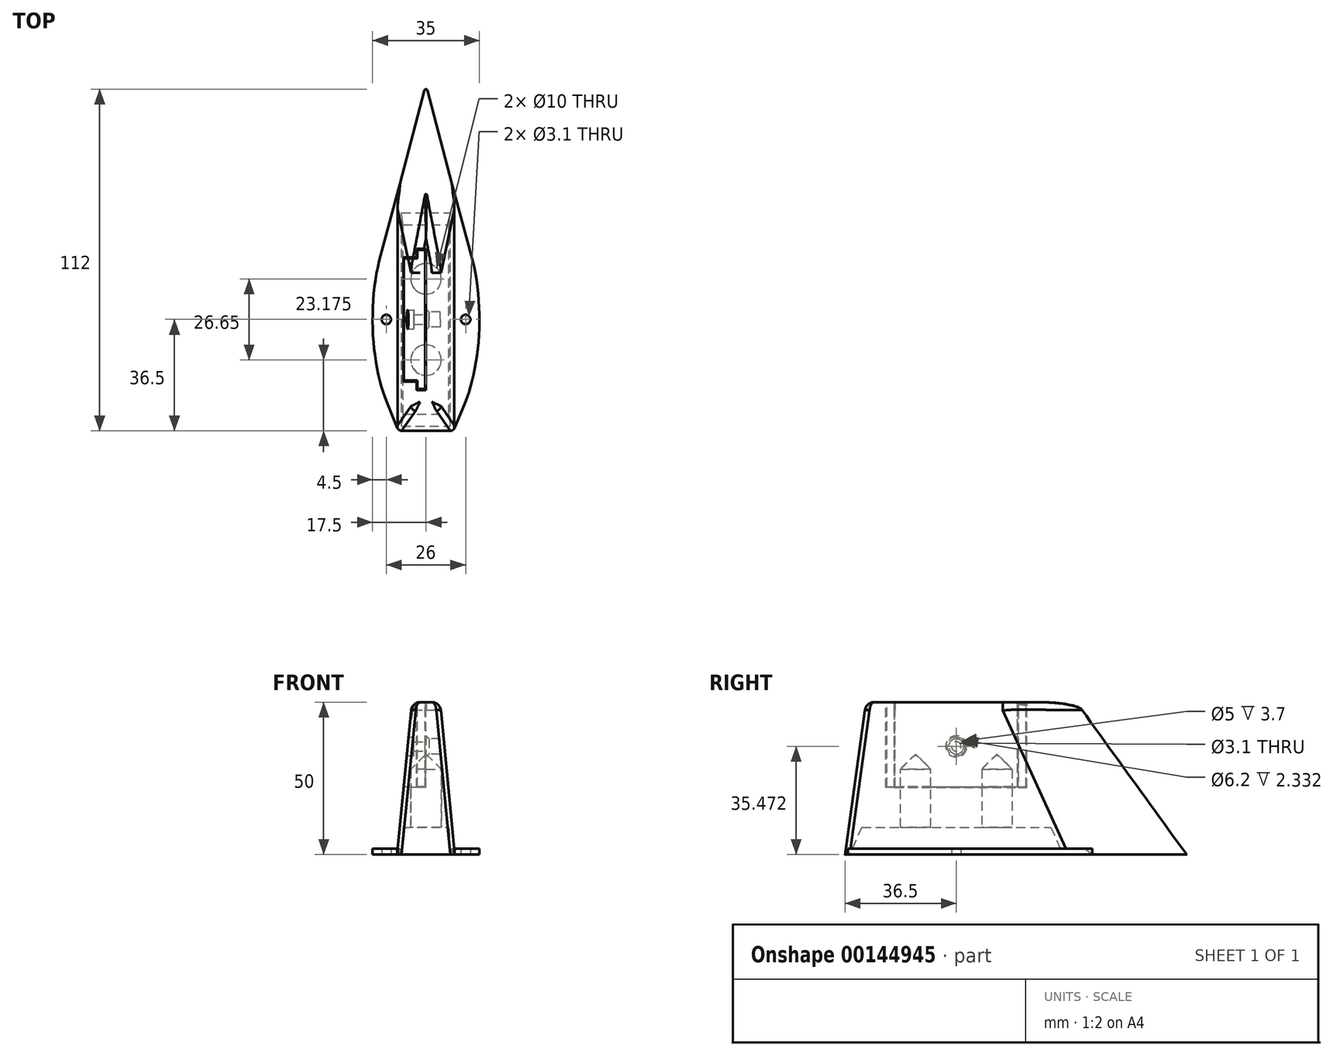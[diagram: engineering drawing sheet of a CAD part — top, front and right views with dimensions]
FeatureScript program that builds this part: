
annotation { "Feature Type Name" : "Feature", "Feature Type Description" : "" }
export const myFeature = defineFeature(function(context is Context, id is Id, definition is map)
    precondition{}
    {
        {
            var Q0;
            Q0=qCreatedBy(makeId("Top.planeOp"),FACE);
            var sketch = newSketch(context, id + "F0", { "sketchPlane" : qUnion([Q0])});
            skPoint(sketch, "E0.middle", {"position": v(0, 0) * mm});
            skLineSegment(sketch, "E1", {"start": v(-0.48, 75.13) * mm, "end": v(-8.52, 44.52) * mm});
            skLineSegment(sketch, "E2.MirrorCS", {"start": v(0.48, 75.13) * mm, "end": v(8.52, 44.52) * mm});
            skPoint(sketch, "E3.visualSharp", {"position": v(0, 76.97) * mm});
            skArc(sketch, "E3.filletArc", {"start": v(0.48, 75.13) * mm, "mid": v(0, 75.5) * mm, "end": v(-0.48, 75.13) * mm});
            skLineSegment(sketch, "E4", {"start": v(-9.5, 36.9) * mm, "end": v(-9.5, -35) * mm});
            skLineSegment(sketch, "E5", {"start": v(-8, -36.5) * mm, "end": v(8, -36.5) * mm});
            skLineSegment(sketch, "E6.MirrorCS", {"start": v(9.5, 36.9) * mm, "end": v(9.5, -35) * mm});
            skPoint(sketch, "E7.visualSharp", {"position": v(-9.5, 40.77) * mm});
            skArc(sketch, "E7.filletArc", {"start": v(-8.52, 44.52) * mm, "mid": v(-9.25, 40.74) * mm, "end": v(-9.5, 36.9) * mm});
            skPoint(sketch, "E8.visualSharp", {"position": v(9.5, 40.77) * mm});
            skArc(sketch, "E8.filletArc", {"start": v(9.5, 36.9) * mm, "mid": v(9.25, 40.74) * mm, "end": v(8.52, 44.52) * mm});
            skPoint(sketch, "E9.visualSharp", {"position": v(9.5, -36.5) * mm});
            skArc(sketch, "E9.filletArc", {"start": v(8, -36.5) * mm, "mid": v(9.06, -36.06) * mm, "end": v(9.5, -35) * mm});
            skPoint(sketch, "E10.visualSharp", {"position": v(-9.5, -36.5) * mm});
            skArc(sketch, "E10.filletArc", {"start": v(-9.5, -35) * mm, "mid": v(-9.06, -36.06) * mm, "end": v(-8, -36.5) * mm});
            skSolve(sketch);
        }
        {
            var Q0;
            Q0=qCreatedBy(makeId("Top.planeOp"),FACE);
            cPlane(context, id + "F1", {"entities" : qUnion([Q0]), "cplaneType" : CPlaneType.OFFSET, "offset" : 50 * mm, "width" : 150 * mm, "height" : 150 * mm});
        }
        {
            var Q0;
            Q0=qCreatedBy(id+"F1.planeOp",FACE);
            var sketch = newSketch(context, id + "F2", { "sketchPlane" : qUnion([Q0])});
            skLineSegment(sketch, "E11", {"start": v(-4.6, 14.01) * mm, "end": v(-4.6, -28.06) * mm});
            skLineSegment(sketch, "E12", {"start": v(-4.26, 17.7) * mm, "end": v(-0.25, 39.13) * mm});
            skLineSegment(sketch, "E13.MirrorCS", {"start": v(4.6, 14.01) * mm, "end": v(4.6, -28.06) * mm});
            skLineSegment(sketch, "E14.MirrorCS", {"start": v(4.26, 17.7) * mm, "end": v(0.25, 39.13) * mm});
            skPoint(sketch, "E15.visualSharp", {"position": v(-4.6, 15.87) * mm});
            skArc(sketch, "E15.filletArc", {"start": v(-4.26, 17.7) * mm, "mid": v(-4.52, 15.86) * mm, "end": v(-4.6, 14.01) * mm});
            skPoint(sketch, "E16.visualSharp", {"position": v(4.6, 15.87) * mm});
            skArc(sketch, "E16.filletArc", {"start": v(4.6, 14.01) * mm, "mid": v(4.52, 15.86) * mm, "end": v(4.26, 17.7) * mm});
            skPoint(sketch, "E17.visualSharp", {"position": v(4.6, -29.56) * mm});
            skArc(sketch, "E17.filletArc", {"start": v(3.1, -29.56) * mm, "mid": v(4.17, -29.12) * mm, "end": v(4.6, -28.06) * mm});
            skPoint(sketch, "E18.visualSharp", {"position": v(-4.6, -29.56) * mm});
            skArc(sketch, "E18.filletArc", {"start": v(-4.6, -28.06) * mm, "mid": v(-4.17, -29.12) * mm, "end": v(-3.1, -29.56) * mm});
            skPoint(sketch, "E19.visualSharp", {"position": v(0, 40.44) * mm});
            skArc(sketch, "E19.filletArc", {"start": v(0.25, 39.13) * mm, "mid": v(0, 39.34) * mm, "end": v(-0.25, 39.13) * mm});
            skLineSegment(sketch, "E20", {"start": v(-3.1, -29.56) * mm, "end": v(3.1, -29.56) * mm});
            skSolve(sketch);
        }
        {
            var Q0;
            Q0 = qSketchRegion(id + "F0", true);
            var Q1;
            Q1 = qSketchRegion(id + "F2", true);
            var Q2;
            Q2=sQuery(id+"F0.wireOp",VERTEX,"E3.filletArc.start");
            var Q3;
            Q3=sQuery(id+"F2.wireOp",VERTEX,"E19.filletArc.start");
            loft(context, id + "F3", {"sheetProfilesArray" : [{ "sheetProfileEntities" : qUnion([Q0]) }, { "sheetProfileEntities" : qUnion([Q1]) }], "matchConnections" : true, "connections" : [{ "connectionEntities" : qUnion([Q2, Q3]), "connectionEdgeQueries" : qUnion([]), "connectionEdgeParameters" : [] }]});
        }
        {
            var Q0;
            Q0=makeQuery(id+"F0.imprint","IMPRINT",FACE,{"disambiguationData":[TD([[makeQuery(id+"F0.imprint","IMPRINT",EDGE,{"derivedFrom":sQuery(id+"F0.wireOp",EDGE,"E1")}),1.0]])]});
            var sketch = newSketch(context, id + "F4", { "sketchPlane" : qUnion([Q0])});
            skLineSegment(sketch, "E21.bottom", {"start": v(-8, -35) * mm, "end": v(8, -35) * mm});
            skLineSegment(sketch, "E21.top", {"start": v(-8, 35) * mm, "end": v(8, 35) * mm});
            skLineSegment(sketch, "E21.left", {"start": v(-8, -35) * mm, "end": v(-8, 35) * mm});
            skLineSegment(sketch, "E21.right", {"start": v(8, -35) * mm, "end": v(8, 35) * mm});
            skPoint(sketch, "E21.middle", {"position": v(0, 0) * mm});
            skSolve(sketch);
        }
        {
            var Q0;
            Q0=makeQuery(id+"F0.imprint","IMPRINT",FACE,{"disambiguationData":[TD([[makeQuery(id+"F0.imprint","IMPRINT",EDGE,{"derivedFrom":sQuery(id+"F0.wireOp",EDGE,"E1")}),1.0]])]});
            cPlane(context, id + "F5", {"entities" : qUnion([Q0]), "cplaneType" : CPlaneType.OFFSET, "offset" : 9 * mm, "width" : 150 * mm, "height" : 150 * mm});
        }
        {
            var Q0;
            Q0=qCreatedBy(id+"F5.planeOp",FACE);
            var sketch = newSketch(context, id + "F6", { "sketchPlane" : qUnion([Q0])});
            skLineSegment(sketch, "E22.bottom", {"start": v(-7.5, -31) * mm, "end": v(7.5, -31) * mm});
            skLineSegment(sketch, "E22.top", {"start": v(-7.5, 31) * mm, "end": v(7.5, 31) * mm});
            skLineSegment(sketch, "E22.left", {"start": v(-7.5, -31) * mm, "end": v(-7.5, 31) * mm});
            skLineSegment(sketch, "E22.right", {"start": v(7.5, -31) * mm, "end": v(7.5, 31) * mm});
            skPoint(sketch, "E22.middle", {"position": v(0, 0) * mm});
            skSolve(sketch);
        }
        {
            var Q1;
            Q1 = qSketchRegion(id + "F6", true);
            var Q2;
            Q2 = qSketchRegion(id + "F4", true);
            loft(context, id + "F7", {"operationType" : NewBodyOperationType.REMOVE, "sheetProfilesArray" : [{ "sheetProfileEntities" : qUnion([Q1]) }, { "sheetProfileEntities" : qUnion([Q2]) }]});
        }
        {
            var Q0;
            Q0=qCreatedBy(makeId("Right.planeOp"),FACE);
            var sketch = newSketch(context, id + "F8", { "sketchPlane" : qUnion([Q0])});
            skLineSegment(sketch, "E23", {"start": v(-13.32, 50) * mm, "end": v(-13.32, 9) * mm});
            skLineSegment(sketch, "E24.MirrorCS", {"start": v(13.32, 50) * mm, "end": v(13.32, 9) * mm});
            skLineSegment(sketch, "E25.bottom", {"start": v(-13.33, 33) * mm, "end": v(-18.33, 33) * mm});
            skLineSegment(sketch, "E25.top", {"start": v(-13.32, 9) * mm, "end": v(-18.32, 9) * mm});
            skLineSegment(sketch, "E25.left", {"start": v(-13.32, 33) * mm, "end": v(-13.32, 9) * mm});
            skLineSegment(sketch, "E25.right", {"start": v(-18.33, 33) * mm, "end": v(-18.32, 9) * mm});
            skLineSegment(sketch, "E26.bottom", {"start": v(-13.33, 33) * mm, "end": v(-16.33, 33) * mm});
            skLineSegment(sketch, "E26.top", {"start": v(-13.33, 50) * mm, "end": v(-16.33, 50) * mm});
            skLineSegment(sketch, "E26.left", {"start": v(-13.33, 33) * mm, "end": v(-13.33, 50) * mm});
            skLineSegment(sketch, "E26.right", {"start": v(-16.33, 33) * mm, "end": v(-16.33, 50) * mm});
            skLineSegment(sketch, "E27.MirrorCS", {"start": v(13.33, 33) * mm, "end": v(18.33, 33) * mm});
            skLineSegment(sketch, "E28.MirrorCS", {"start": v(18.33, 33) * mm, "end": v(18.32, 9) * mm});
            skLineSegment(sketch, "E29.MirrorCS", {"start": v(13.33, 33) * mm, "end": v(16.33, 33) * mm});
            skLineSegment(sketch, "E30.MirrorCS", {"start": v(13.32, 33) * mm, "end": v(13.32, 9) * mm});
            skLineSegment(sketch, "E31.MirrorCS", {"start": v(13.33, 50) * mm, "end": v(16.33, 50) * mm});
            skLineSegment(sketch, "E32.MirrorCS", {"start": v(13.33, 33) * mm, "end": v(13.33, 50) * mm});
            skLineSegment(sketch, "E33.MirrorCS", {"start": v(16.33, 33) * mm, "end": v(16.33, 50) * mm});
            skLineSegment(sketch, "E34.MirrorCS", {"start": v(13.32, 9) * mm, "end": v(18.32, 9) * mm});
            skSolve(sketch);
        }
        {
            var Q0;
            Q0=makeQuery(id+"F8.imprint","IMPRINT",FACE,{"disambiguationData":[TD([[makeQuery(id+"F8.imprint","IMPRINT",EDGE,{"derivedFrom":sQuery(id+"F8.wireOp",EDGE,"E26.bottom")}),-1.0]])]});
            var Q1;
            Q1=makeQuery(id+"F8.imprint","IMPRINT",FACE,{"disambiguationData":[TD([[makeQuery(id+"F8.imprint","IMPRINT",EDGE,{"derivedFrom":sQuery(id+"F8.wireOp",EDGE,"E25.bottom")}),1.0]])]});
            var Q2;
            Q2=sQuery(id+"F8.wireOp",EDGE,"E26.left");
            revolve(context, id + "F9", {"operationType" : NewBodyOperationType.REMOVE, "entities" : qUnion([Q0, Q1]), "axis" : qUnion([Q2]), "revolveType" : RevolveType.FULL, "oppositeDirection" : true});
        }
        {
            var Q0;
            Q0=makeQuery(id+"F8.imprint","IMPRINT",FACE,{"disambiguationData":[TD([[makeQuery(id+"F8.imprint","IMPRINT",EDGE,{"derivedFrom":sQuery(id+"F8.wireOp",EDGE,"E27.MirrorCS")}),-1.0]])]});
            var Q1;
            Q1=makeQuery(id+"F8.imprint","IMPRINT",FACE,{"disambiguationData":[TD([[makeQuery(id+"F8.imprint","IMPRINT",EDGE,{"derivedFrom":sQuery(id+"F8.wireOp",EDGE,"E29.MirrorCS")}),1.0]])]});
            var Q2;
            Q2=sQuery(id+"F8.wireOp",EDGE,"E24.MirrorCS");
            revolve(context, id + "F10", {"operationType" : NewBodyOperationType.REMOVE, "entities" : qUnion([Q0, Q1]), "axis" : qUnion([Q2]), "revolveType" : RevolveType.FULL, "oppositeDirection" : true});
        }
        {
            var Q0;
            Q0=makeQuery(id+"F3.opLoft","MID_CAP_EDGE",EDGE,{"disambiguationData":[OSD([sQuery(id+"F2.wireOp",EDGE,"E13.MirrorCS"),sQuery(id+"F2.wireOp",EDGE,"E16.filletArc"),sQuery(id+"F2.wireOp",EDGE,"E17.filletArc")])],"capPos":1.0});
            fillet(context, id + "F11", {"entities" : qUnion([Q0]), "radius" : 3 * mm, "tangentPropagation" : true, "allowEdgeOverflow" : false});
        }
        {
            var Q0;
            Q0=makeQuery(id+"F3.opLoft","CAP_FACE",FACE,{"disambiguationData":[OSD([makeQuery(id+"F0.imprint","IMPRINT",FACE,{"disambiguationData":[TD([[makeQuery(id+"F0.imprint","IMPRINT",EDGE,{"derivedFrom":sQuery(id+"F0.wireOp",EDGE,"E1")}),1.0]])]})])],"isStart":true});
            var sketch = newSketch(context, id + "F12", { "sketchPlane" : qUnion([Q0])});
            skCircle(sketch, "E35", {"center": v(13, 0) * mm, "radius": 1.55 * mm});
            skCircle(sketch, "E36.MirrorC", {"center": v(-13, 0) * mm, "radius": 1.55 * mm});
            skFitSpline(sketch, "E37.0", {"points": [v(9.5, -36.9) * mm, v(9.5, -37.51) * mm, v(9.46, -38.8) * mm, v(9.2, -41.45) * mm, v(8.82, -43.38) * mm, v(8.52, -44.52) * mm]});
            skFitSpline(sketch, "E38.0", {"points": [v(-8.52, -44.52) * mm, v(-8.82, -43.38) * mm, v(-9.2, -41.45) * mm, v(-9.46, -38.8) * mm, v(-9.5, -37.51) * mm, v(-9.5, -36.9) * mm]});
            skLineSegment(sketch, "E39.0", {"start": v(-9.5, -36.9) * mm, "end": v(-9.5, 35) * mm});
            skFitSpline(sketch, "E40.0", {"points": [v(8, 36.5) * mm, v(8.25, 36.5) * mm, v(8.67, 36.38) * mm, v(9.1, 36.06) * mm, v(9.4, 35.62) * mm, v(9.5, 35.23) * mm, v(9.5, 35) * mm]});
            skFitSpline(sketch, "E41.0", {"points": [v(-9.5, 35) * mm, v(-9.5, 35.23) * mm, v(-9.4, 35.62) * mm, v(-9.1, 36.06) * mm, v(-8.67, 36.38) * mm, v(-8.25, 36.5) * mm, v(-8, 36.5) * mm]});
            skEllipticalArc(sketch, "E42", {});
            skLineSegment(sketch, "E43", {"start": v(8.52, -44.52) * mm, "end": v(14.87, -21.07) * mm});
            skLineSegment(sketch, "E44.MirrorCS", {"start": v(-8.52, -44.52) * mm, "end": v(-14.87, -21.07) * mm});
            skLineSegment(sketch, "E45", {"start": v(12.75, 27.4) * mm, "end": v(9.39, 35.57) * mm});
            skLineSegment(sketch, "E46.MirrorCS", {"start": v(-12.75, 27.4) * mm, "end": v(-9.39, 35.57) * mm});
            skPoint(sketch, "E47.orphan", {"position": v(-8, 36.5) * mm});
            skPoint(sketch, "E48.orphan", {"position": v(8, 36.5) * mm});
            skEllipticalArc(sketch, "E49.trimOffspring", {});
            skLineSegment(sketch, "E50.0", {"start": v(9, 35) * mm, "end": v(9, -36.9) * mm});
            skLineSegment(sketch, "E51", {"start": v(9.39, 35.57) * mm, "end": v(9, 35) * mm});
            skLineSegment(sketch, "E52", {"start": v(8.52, -44.52) * mm, "end": v(9, -36.9) * mm});
            skLineSegment(sketch, "E53.MirrorCS", {"start": v(-9, 35) * mm, "end": v(-9, -36.9) * mm});
            skLineSegment(sketch, "E54.MirrorCS", {"start": v(-8.52, -44.52) * mm, "end": v(-9, -36.9) * mm});
            skLineSegment(sketch, "E55.MirrorCS", {"start": v(-9.39, 35.57) * mm, "end": v(-9, 35) * mm});
            const initialGuessF12  = {"E42": [0, 0, 0, 1, 0.04, 0.0175, 0.8160046856801231, 2.1256548198851757], "E49.trimOffspring": [0, 0, 0, 1, 0.04, 0.0175, 4.1575304872944105, 5.467180621499463]};
            skSetInitialGuess(sketch, initialGuessF12);
            skSolve(sketch);
        }
        {
            var Q0;
            Q0 = qSketchRegion(id + "F12", true);
            extrude(context, id + "F13", {"entities" : qUnion([Q0]), "operationType" : NewBodyOperationType.ADD, "oppositeDirection" : true, "depth" : 2 * mm});
        }
        {
            var Q0;
            Q0=makeQuery(id+"F10.boolean.opBoolean","COPY",EDGE,{"derivedFrom":makeQuery(id+"F10.opRevolve","SWEPT_EDGE",EDGE,{"disambiguationData":[OSD([sQuery(id+"F8.wireOp",EDGE,"E27.MirrorCS"),sQuery(id+"F8.wireOp",EDGE,"E29.MirrorCS"),sQuery(id+"F8.wireOp",EDGE,"E33.MirrorCS")])]})});
            var Q1;
            Q1=makeQuery(id+"F9.boolean.opBoolean","COPY",EDGE,{"derivedFrom":makeQuery(id+"F9.opRevolve","SWEPT_EDGE",EDGE,{"disambiguationData":[OSD([sQuery(id+"F8.wireOp",EDGE,"E25.bottom"),sQuery(id+"F8.wireOp",EDGE,"E26.bottom"),sQuery(id+"F8.wireOp",EDGE,"E26.right")])]})});
            chamfer(context, id + "F14", {"entities" : qUnion([Q0, Q1]), "width" : 5 * mm, "tangentPropagation" : true});
        }
        {
            var Q0;
            Q0=makeQuery(id+"F11.opFillet","SPLIT",FACE,{"disambiguationData":[OD(2.0)],"derivedFrom":makeQuery(id+"F3.opLoft","CAP_FACE",FACE,{"disambiguationData":[OSD([makeQuery(id+"F2.imprint","IMPRINT",FACE,{"disambiguationData":[TD([[makeQuery(id+"F2.imprint","IMPRINT",EDGE,{"derivedFrom":sQuery(id+"F2.wireOp",EDGE,"E11")}),1.0]])]})])],"isStart":true})});
            var sketch = newSketch(context, id + "F15", { "sketchPlane" : qUnion([Q0])});
            skLineSegment(sketch, "E56.left", {"start": v(0, 20.7) * mm, "end": v(0, -20.3) * mm});
            skLineSegment(sketch, "E56.right", {"start": v(-0.3, 20.3) * mm, "end": v(-0.3, -20.3) * mm});
            skLineSegment(sketch, "E57", {"start": v(0, 22.84) * mm, "end": v(0, 20.7) * mm});
            skLineSegment(sketch, "E58", {"start": v(-0.3, 20.3) * mm, "end": v(-0.3, 22.8) * mm});
            skLineSegment(sketch, "E59", {"start": v(-0.3, 22.8) * mm, "end": v(-2.8, 22.8) * mm});
            skLineSegment(sketch, "E60", {"start": v(-2.8, 22.8) * mm, "end": v(-2.8, 20.3) * mm});
            skLineSegment(sketch, "E61", {"start": v(-3.1, 20.34) * mm, "end": v(-3.1, 23.14) * mm});
            skLineSegment(sketch, "E62", {"start": v(0, 22.84) * mm, "end": v(0, 23.14) * mm});
            skLineSegment(sketch, "E63", {"start": v(0, 23.14) * mm, "end": v(-3.1, 23.14) * mm});
            skLineSegment(sketch, "E64", {"start": v(-3.1, 20.34) * mm, "end": v(-10.14, 20.34) * mm});
            skLineSegment(sketch, "E65", {"start": v(-10.14, 20.34) * mm, "end": v(-10.14, 20.04) * mm});
            skLineSegment(sketch, "E66", {"start": v(-10.14, 20.04) * mm, "end": v(-2.8, 20.04) * mm});
            skLineSegment(sketch, "E67", {"start": v(-2.8, 20.04) * mm, "end": v(-2.8, 20.3) * mm});
            skLineSegment(sketch, "E68.MirrorCS", {"start": v(0, -22.84) * mm, "end": v(0, -23.14) * mm});
            skLineSegment(sketch, "E69.MirrorCS", {"start": v(-2.8, -20.04) * mm, "end": v(-2.8, -20.3) * mm});
            skLineSegment(sketch, "E70.MirrorCS", {"start": v(-10.14, -20.34) * mm, "end": v(-10.14, -20.04) * mm});
            skLineSegment(sketch, "E71.MirrorCS", {"start": v(-3.1, -20.34) * mm, "end": v(-3.1, -23.14) * mm});
            skLineSegment(sketch, "E72.MirrorCS", {"start": v(0, -22.84) * mm, "end": v(0, -20.7) * mm});
            skLineSegment(sketch, "E73.MirrorCS", {"start": v(0, -23.14) * mm, "end": v(-3.1, -23.14) * mm});
            skLineSegment(sketch, "E74.MirrorCS", {"start": v(-0.3, -20.3) * mm, "end": v(-0.3, -22.8) * mm});
            skLineSegment(sketch, "E75.MirrorCS", {"start": v(-2.8, -22.8) * mm, "end": v(-2.8, -20.3) * mm});
            skLineSegment(sketch, "E76.MirrorCS", {"start": v(-3.1, -20.34) * mm, "end": v(-10.14, -20.34) * mm});
            skLineSegment(sketch, "E77.MirrorCS", {"start": v(-10.14, -20.04) * mm, "end": v(-2.8, -20.04) * mm});
            skLineSegment(sketch, "E78.MirrorCS", {"start": v(-0.3, -22.8) * mm, "end": v(-2.8, -22.8) * mm});
            skLineSegment(sketch, "E79", {"start": v(0, -20.3) * mm, "end": v(0, -20.7) * mm});
            skSolve(sketch);
        }
        {
            var Q0;
            Q0 = qSketchRegion(id + "F15", true);
            extrude(context, id + "F16", {"entities" : qUnion([Q0]), "operationType" : NewBodyOperationType.REMOVE, "oppositeDirection" : true, "depth" : 28 * mm});
        }
        {
            var Q0;
            {var subQ0=sQuery(id+"F15.wireOp",EDGE,"E74.MirrorCS");var subQ1=sQuery(id+"F15.wireOp",EDGE,"E58");var subQ2=sQuery(id+"F15.wireOp",EDGE,"E56.right");var subQ3=sQuery(id+"F15.wireOp",EDGE,"E73.MirrorCS");var subQ4=sQuery(id+"F15.wireOp",EDGE,"E79");var subQ5=sQuery(id+"F15.wireOp",EDGE,"E72.MirrorCS");var subQ6=sQuery(id+"F15.wireOp",EDGE,"E68.MirrorCS");var subQ7=sQuery(id+"F15.wireOp",EDGE,"E62");var subQ8=sQuery(id+"F15.wireOp",EDGE,"E57");var subQ9=sQuery(id+"F15.wireOp",EDGE,"E56.left");var subQ10=sQuery(id+"F15.wireOp",EDGE,"E71.MirrorCS");var subQ11=sQuery(id+"F15.wireOp",EDGE,"E75.MirrorCS");var subQ12=sQuery(id+"F15.wireOp",EDGE,"E69.MirrorCS");var subQ13=sQuery(id+"F15.wireOp",EDGE,"E76.MirrorCS");var subQ14=sQuery(id+"F15.wireOp",EDGE,"E77.MirrorCS");var subQ15=sQuery(id+"F15.wireOp",EDGE,"E78.MirrorCS");Q0=makeQuery(id+"F16.boolean.opBoolean","COPY",FACE,{"disambiguationData":[TD([makeQuery(id+"F3.opLoft","SWEPT_FACE",FACE,{"disambiguationData":[OSD([sQuery(id+"F0.wireOp",EDGE,"E4"),sQuery(id+"F0.wireOp",EDGE,"E7.filletArc"),sQuery(id+"F0.wireOp",EDGE,"E10.filletArc"),sQuery(id+"F2.wireOp",EDGE,"E11"),sQuery(id+"F2.wireOp",EDGE,"E15.filletArc"),sQuery(id+"F2.wireOp",EDGE,"E18.filletArc")])]}),makeQuery(id+"F9.boolean.opBoolean","COPY",FACE,{"derivedFrom":makeQuery(id+"F9.opRevolve","SWEPT_FACE",FACE,{"disambiguationData":[OSD([sQuery(id+"F8.wireOp",EDGE,"E25.right")])]})}),makeQuery(id+"F16.opExtrude","SWEPT_FACE",FACE,{"disambiguationData":[OSD([subQ9,subQ8,subQ7,subQ6,subQ5,subQ4])]}),makeQuery(id+"F16.opExtrude","SWEPT_FACE",FACE,{"disambiguationData":[OSD([subQ2,subQ1,subQ0])]}),makeQuery(id+"F16.opExtrude","SWEPT_FACE",FACE,{"disambiguationData":[OSD([subQ12,subQ11])]}),makeQuery(id+"F16.opExtrude","SWEPT_FACE",FACE,{"disambiguationData":[OSD([subQ10])]}),makeQuery(id+"F16.opExtrude","SWEPT_FACE",FACE,{"disambiguationData":[OSD([subQ3])]}),makeQuery(id+"F16.opExtrude","SWEPT_FACE",FACE,{"disambiguationData":[OSD([subQ13])]}),makeQuery(id+"F16.opExtrude","SWEPT_FACE",FACE,{"disambiguationData":[OSD([subQ14])]}),makeQuery(id+"F16.opExtrude","SWEPT_FACE",FACE,{"disambiguationData":[OSD([subQ15])]})])],"derivedFrom":makeQuery(id+"F16.opExtrude","CAP_FACE",FACE,{"disambiguationData":[OSD([subQ9,subQ2,subQ8,subQ1,sQuery(id+"F15.wireOp",EDGE,"E59"),sQuery(id+"F15.wireOp",EDGE,"E60"),sQuery(id+"F15.wireOp",EDGE,"E61"),subQ7,sQuery(id+"F15.wireOp",EDGE,"E63"),sQuery(id+"F15.wireOp",EDGE,"E64"),sQuery(id+"F15.wireOp",EDGE,"E65"),sQuery(id+"F15.wireOp",EDGE,"E66"),sQuery(id+"F15.wireOp",EDGE,"E67"),subQ6,subQ12,sQuery(id+"F15.wireOp",EDGE,"E70.MirrorCS"),subQ10,subQ5,subQ3,subQ0,subQ11,subQ13,subQ14,subQ15,subQ4])],"isStart":false})});}
            var sketch = newSketch(context, id + "F17", { "sketchPlane" : qUnion([Q0])});
            skLineSegment(sketch, "E80", {"start": v(-2.8, -20.04) * mm, "end": v(-10.13, -20.04) * mm});
            skPoint(sketch, "E80.endSnap0", {"position": v(-5.07, -20.04) * mm});
            skLineSegment(sketch, "E81", {"start": v(-10.13, -20.04) * mm, "end": v(-10.13, 20.04) * mm});
            skLineSegment(sketch, "E82", {"start": v(-10.13, 20.04) * mm, "end": v(-2.8, 20.04) * mm});
            skLineSegment(sketch, "E83", {"start": v(-2.8, 20.04) * mm, "end": v(-2.8, 22.8) * mm});
            skLineSegment(sketch, "E84", {"start": v(-2.8, 22.8) * mm, "end": v(-0.3, 22.8) * mm});
            skLineSegment(sketch, "E85", {"start": v(-0.3, 22.8) * mm, "end": v(-0.3, -22.8) * mm});
            skLineSegment(sketch, "E86", {"start": v(-0.3, -22.8) * mm, "end": v(-2.8, -22.8) * mm});
            skLineSegment(sketch, "E87", {"start": v(-2.8, -22.8) * mm, "end": v(-2.8, -20.04) * mm});
            skSolve(sketch);
        }
        {
            var Q0;
            Q0 = qSketchRegion(id + "F17", true);
            extrude(context, id + "F18", {"entities" : qUnion([Q0]), "operationType" : NewBodyOperationType.REMOVE, "depth" : .3 * mm});
        }
        {
            var Q0;
            {var subQ0=sQuery(id+"F8.wireOp",EDGE,"E26.right");var subQ1=sQuery(id+"F15.wireOp",EDGE,"E74.MirrorCS");var subQ2=sQuery(id+"F15.wireOp",EDGE,"E58");var subQ3=sQuery(id+"F15.wireOp",EDGE,"E56.right");var subQ4=sQuery(id+"F8.wireOp",EDGE,"E33.MirrorCS");Q0=makeQuery(id+"F16.boolean.opBoolean","COPY",FACE,{"disambiguationData":[TD([makeQuery(id+"F3.opLoft","CAP_FACE",FACE,{"disambiguationData":[OSD([makeQuery(id+"F2.imprint","IMPRINT",FACE,{"disambiguationData":[TD([[makeQuery(id+"F2.imprint","IMPRINT",EDGE,{"derivedFrom":sQuery(id+"F2.wireOp",EDGE,"E11")}),1.0]])]})])],"isStart":true}),makeQuery(id+"F9.boolean.opBoolean","COPY",FACE,{"derivedFrom":makeQuery(id+"F9.opRevolve","SWEPT_FACE",FACE,{"disambiguationData":[OSD([sQuery(id+"F8.wireOp",EDGE,"E25.right")])]})}),makeQuery(id+"F9.boolean.opBoolean","COPY",FACE,{"derivedFrom":makeQuery(id+"F9.opRevolve","SWEPT_FACE",FACE,{"disambiguationData":[OSD([subQ0])]})}),makeQuery(id+"F10.boolean.opBoolean","COPY",FACE,{"derivedFrom":makeQuery(id+"F10.opRevolve","SWEPT_FACE",FACE,{"disambiguationData":[OSD([sQuery(id+"F8.wireOp",EDGE,"E28.MirrorCS")])]})}),makeQuery(id+"F10.boolean.opBoolean","COPY",FACE,{"derivedFrom":makeQuery(id+"F10.opRevolve","SWEPT_FACE",FACE,{"disambiguationData":[OSD([subQ4])]})}),makeQuery(id+"F14.opChamfer","BLEND_FACE",FACE,{"disambiguationData":[OSD([sQuery(id+"F8.wireOp",EDGE,"E25.bottom"),sQuery(id+"F8.wireOp",EDGE,"E26.bottom"),subQ0])]}),makeQuery(id+"F14.opChamfer","BLEND_FACE",FACE,{"disambiguationData":[OSD([sQuery(id+"F8.wireOp",EDGE,"E27.MirrorCS"),sQuery(id+"F8.wireOp",EDGE,"E29.MirrorCS"),subQ4])]}),makeQuery(id+"F16.opExtrude","CAP_FACE",FACE,{"disambiguationData":[OSD([sQuery(id+"F15.wireOp",EDGE,"E56.left"),subQ3,sQuery(id+"F15.wireOp",EDGE,"E57"),subQ2,sQuery(id+"F15.wireOp",EDGE,"E59"),sQuery(id+"F15.wireOp",EDGE,"E60"),sQuery(id+"F15.wireOp",EDGE,"E61"),sQuery(id+"F15.wireOp",EDGE,"E62"),sQuery(id+"F15.wireOp",EDGE,"E63"),sQuery(id+"F15.wireOp",EDGE,"E64"),sQuery(id+"F15.wireOp",EDGE,"E65"),sQuery(id+"F15.wireOp",EDGE,"E66"),sQuery(id+"F15.wireOp",EDGE,"E67"),sQuery(id+"F15.wireOp",EDGE,"E68.MirrorCS"),sQuery(id+"F15.wireOp",EDGE,"E69.MirrorCS"),sQuery(id+"F15.wireOp",EDGE,"E70.MirrorCS"),sQuery(id+"F15.wireOp",EDGE,"E71.MirrorCS"),sQuery(id+"F15.wireOp",EDGE,"E72.MirrorCS"),sQuery(id+"F15.wireOp",EDGE,"E73.MirrorCS"),subQ1,sQuery(id+"F15.wireOp",EDGE,"E75.MirrorCS"),sQuery(id+"F15.wireOp",EDGE,"E76.MirrorCS"),sQuery(id+"F15.wireOp",EDGE,"E77.MirrorCS"),sQuery(id+"F15.wireOp",EDGE,"E78.MirrorCS"),sQuery(id+"F15.wireOp",EDGE,"E79")])],"isStart":false})])],"derivedFrom":makeQuery(id+"F16.opExtrude","SWEPT_FACE",FACE,{"disambiguationData":[OSD([subQ3,subQ2,subQ1])]})});}
            var sketch = newSketch(context, id + "F19", { "sketchPlane" : qUnion([Q0])});
            skCircle(sketch, "E88", {"center": v(0, 35.47) * mm, "radius": 1.55 * mm});
            skSolve(sketch);
        }
        {
            var Q0;
            Q0 = qSketchRegion(id + "F19", true);
            extrude(context, id + "F20", {"entities" : qUnion([Q0]), "operationType" : NewBodyOperationType.REMOVE, "oppositeDirection" : true, "depth" : 25 * mm});
        }
        {
            var Q0;
            {var subQ0=sQuery(id+"F8.wireOp",EDGE,"E26.right");var subQ1=sQuery(id+"F15.wireOp",EDGE,"E74.MirrorCS");var subQ2=sQuery(id+"F15.wireOp",EDGE,"E58");var subQ3=sQuery(id+"F15.wireOp",EDGE,"E56.right");var subQ4=sQuery(id+"F8.wireOp",EDGE,"E33.MirrorCS");Q0=makeQuery(id+"F16.boolean.opBoolean","COPY",FACE,{"disambiguationData":[TD([makeQuery(id+"F3.opLoft","CAP_FACE",FACE,{"disambiguationData":[OSD([makeQuery(id+"F2.imprint","IMPRINT",FACE,{"disambiguationData":[TD([[makeQuery(id+"F2.imprint","IMPRINT",EDGE,{"derivedFrom":sQuery(id+"F2.wireOp",EDGE,"E11")}),1.0]])]})])],"isStart":true}),makeQuery(id+"F9.boolean.opBoolean","COPY",FACE,{"derivedFrom":makeQuery(id+"F9.opRevolve","SWEPT_FACE",FACE,{"disambiguationData":[OSD([sQuery(id+"F8.wireOp",EDGE,"E25.right")])]})}),makeQuery(id+"F9.boolean.opBoolean","COPY",FACE,{"derivedFrom":makeQuery(id+"F9.opRevolve","SWEPT_FACE",FACE,{"disambiguationData":[OSD([subQ0])]})}),makeQuery(id+"F10.boolean.opBoolean","COPY",FACE,{"derivedFrom":makeQuery(id+"F10.opRevolve","SWEPT_FACE",FACE,{"disambiguationData":[OSD([sQuery(id+"F8.wireOp",EDGE,"E28.MirrorCS")])]})}),makeQuery(id+"F10.boolean.opBoolean","COPY",FACE,{"derivedFrom":makeQuery(id+"F10.opRevolve","SWEPT_FACE",FACE,{"disambiguationData":[OSD([subQ4])]})}),makeQuery(id+"F14.opChamfer","BLEND_FACE",FACE,{"disambiguationData":[OSD([sQuery(id+"F8.wireOp",EDGE,"E25.bottom"),sQuery(id+"F8.wireOp",EDGE,"E26.bottom"),subQ0])]}),makeQuery(id+"F14.opChamfer","BLEND_FACE",FACE,{"disambiguationData":[OSD([sQuery(id+"F8.wireOp",EDGE,"E27.MirrorCS"),sQuery(id+"F8.wireOp",EDGE,"E29.MirrorCS"),subQ4])]}),makeQuery(id+"F16.opExtrude","CAP_FACE",FACE,{"disambiguationData":[OSD([sQuery(id+"F15.wireOp",EDGE,"E56.left"),subQ3,sQuery(id+"F15.wireOp",EDGE,"E57"),subQ2,sQuery(id+"F15.wireOp",EDGE,"E59"),sQuery(id+"F15.wireOp",EDGE,"E60"),sQuery(id+"F15.wireOp",EDGE,"E61"),sQuery(id+"F15.wireOp",EDGE,"E62"),sQuery(id+"F15.wireOp",EDGE,"E63"),sQuery(id+"F15.wireOp",EDGE,"E64"),sQuery(id+"F15.wireOp",EDGE,"E65"),sQuery(id+"F15.wireOp",EDGE,"E66"),sQuery(id+"F15.wireOp",EDGE,"E67"),sQuery(id+"F15.wireOp",EDGE,"E68.MirrorCS"),sQuery(id+"F15.wireOp",EDGE,"E69.MirrorCS"),sQuery(id+"F15.wireOp",EDGE,"E70.MirrorCS"),sQuery(id+"F15.wireOp",EDGE,"E71.MirrorCS"),sQuery(id+"F15.wireOp",EDGE,"E72.MirrorCS"),sQuery(id+"F15.wireOp",EDGE,"E73.MirrorCS"),subQ1,sQuery(id+"F15.wireOp",EDGE,"E75.MirrorCS"),sQuery(id+"F15.wireOp",EDGE,"E76.MirrorCS"),sQuery(id+"F15.wireOp",EDGE,"E77.MirrorCS"),sQuery(id+"F15.wireOp",EDGE,"E78.MirrorCS"),sQuery(id+"F15.wireOp",EDGE,"E79")])],"isStart":false})])],"derivedFrom":makeQuery(id+"F16.opExtrude","SWEPT_FACE",FACE,{"disambiguationData":[OSD([subQ3,subQ2,subQ1])]})});}
            var sketch = newSketch(context, id + "F21", { "sketchPlane" : qUnion([Q0])});
            skCircle(sketch, "E89", {"center": v(0, 35.47) * mm, "radius": 2.5 * mm});
            skSolve(sketch);
        }
        {
            var Q0;
            Q0 = qSketchRegion(id + "F21", true);
            extrude(context, id + "F22", {"entities" : qUnion([Q0]), "operationType" : NewBodyOperationType.REMOVE, "depth" : 5 * mm});
        }
        {
            var Q0;
            Q0=qCreatedBy(makeId("Right.planeOp"),FACE);
            cPlane(context, id + "F23", {"entities" : qUnion([Q0]), "cplaneType" : CPlaneType.OFFSET, "offset" : 4 * mm, "oppositeDirection" : true, "width" : 150 * mm, "height" : 150 * mm});
        }
        {
            var Q0;
            Q0=qCreatedBy(id+"F23.planeOp",FACE);
            var sketch = newSketch(context, id + "F24", { "sketchPlane" : qUnion([Q0])});
            skCircle(sketch, "E90", {"center": v(0, 35.47) * mm, "radius": 3.1 * mm});
            skSolve(sketch);
        }
        {
            var Q0;
            Q0 = qSketchRegion(id + "F24", true);
            extrude(context, id + "F25", {"entities" : qUnion([Q0]), "operationType" : NewBodyOperationType.REMOVE, "oppositeDirection" : true, "depth" : 25 * mm});
        }
        {
            var Q0;
            {var subQ0=sQuery(id+"F8.wireOp",EDGE,"E26.right");var subQ1=sQuery(id+"F15.wireOp",EDGE,"E79");var subQ2=sQuery(id+"F15.wireOp",EDGE,"E72.MirrorCS");var subQ3=sQuery(id+"F15.wireOp",EDGE,"E68.MirrorCS");var subQ4=sQuery(id+"F15.wireOp",EDGE,"E62");var subQ5=sQuery(id+"F15.wireOp",EDGE,"E57");var subQ6=sQuery(id+"F15.wireOp",EDGE,"E56.left");var subQ7=sQuery(id+"F8.wireOp",EDGE,"E33.MirrorCS");Q0=makeQuery(id+"F22.boolean.opBoolean","INTERSECT",EDGE,{"derivedFrom":[makeQuery(id+"F16.boolean.opBoolean","COPY",FACE,{"disambiguationData":[TD([makeQuery(id+"F3.opLoft","CAP_FACE",FACE,{"disambiguationData":[OSD([makeQuery(id+"F2.imprint","IMPRINT",FACE,{"disambiguationData":[TD([[makeQuery(id+"F2.imprint","IMPRINT",EDGE,{"derivedFrom":sQuery(id+"F2.wireOp",EDGE,"E11")}),1.0]])]})])],"isStart":true}),makeQuery(id+"F9.boolean.opBoolean","COPY",FACE,{"derivedFrom":makeQuery(id+"F9.opRevolve","SWEPT_FACE",FACE,{"disambiguationData":[OSD([sQuery(id+"F8.wireOp",EDGE,"E25.right")])]})}),makeQuery(id+"F9.boolean.opBoolean","COPY",FACE,{"derivedFrom":makeQuery(id+"F9.opRevolve","SWEPT_FACE",FACE,{"disambiguationData":[OSD([subQ0])]})}),makeQuery(id+"F10.boolean.opBoolean","COPY",FACE,{"derivedFrom":makeQuery(id+"F10.opRevolve","SWEPT_FACE",FACE,{"disambiguationData":[OSD([sQuery(id+"F8.wireOp",EDGE,"E28.MirrorCS")])]})}),makeQuery(id+"F10.boolean.opBoolean","COPY",FACE,{"derivedFrom":makeQuery(id+"F10.opRevolve","SWEPT_FACE",FACE,{"disambiguationData":[OSD([subQ7])]})}),makeQuery(id+"F14.opChamfer","BLEND_FACE",FACE,{"disambiguationData":[OSD([sQuery(id+"F8.wireOp",EDGE,"E25.bottom"),sQuery(id+"F8.wireOp",EDGE,"E26.bottom"),subQ0])]}),makeQuery(id+"F14.opChamfer","BLEND_FACE",FACE,{"disambiguationData":[OSD([sQuery(id+"F8.wireOp",EDGE,"E27.MirrorCS"),sQuery(id+"F8.wireOp",EDGE,"E29.MirrorCS"),subQ7])]}),makeQuery(id+"F16.opExtrude","CAP_FACE",FACE,{"disambiguationData":[OSD([subQ6,sQuery(id+"F15.wireOp",EDGE,"E56.right"),subQ5,sQuery(id+"F15.wireOp",EDGE,"E58"),sQuery(id+"F15.wireOp",EDGE,"E59"),sQuery(id+"F15.wireOp",EDGE,"E60"),sQuery(id+"F15.wireOp",EDGE,"E61"),subQ4,sQuery(id+"F15.wireOp",EDGE,"E63"),sQuery(id+"F15.wireOp",EDGE,"E64"),sQuery(id+"F15.wireOp",EDGE,"E65"),sQuery(id+"F15.wireOp",EDGE,"E66"),sQuery(id+"F15.wireOp",EDGE,"E67"),subQ3,sQuery(id+"F15.wireOp",EDGE,"E69.MirrorCS"),sQuery(id+"F15.wireOp",EDGE,"E70.MirrorCS"),sQuery(id+"F15.wireOp",EDGE,"E71.MirrorCS"),subQ2,sQuery(id+"F15.wireOp",EDGE,"E73.MirrorCS"),sQuery(id+"F15.wireOp",EDGE,"E74.MirrorCS"),sQuery(id+"F15.wireOp",EDGE,"E75.MirrorCS"),sQuery(id+"F15.wireOp",EDGE,"E76.MirrorCS"),sQuery(id+"F15.wireOp",EDGE,"E77.MirrorCS"),sQuery(id+"F15.wireOp",EDGE,"E78.MirrorCS"),subQ1])],"isStart":false})])],"derivedFrom":makeQuery(id+"F16.opExtrude","SWEPT_FACE",FACE,{"disambiguationData":[OSD([subQ6,subQ5,subQ4,subQ3,subQ2,subQ1])]})}),makeQuery(id+"F22.opExtrude","SWEPT_FACE",FACE,{"disambiguationData":[OSD([sQuery(id+"F21.wireOp",EDGE,"E89")])]})]});}
            chamfer(context, id + "F26", {"entities" : qUnion([Q0]), "width" : 1 * mm, "tangentPropagation" : true});
        }
    });
